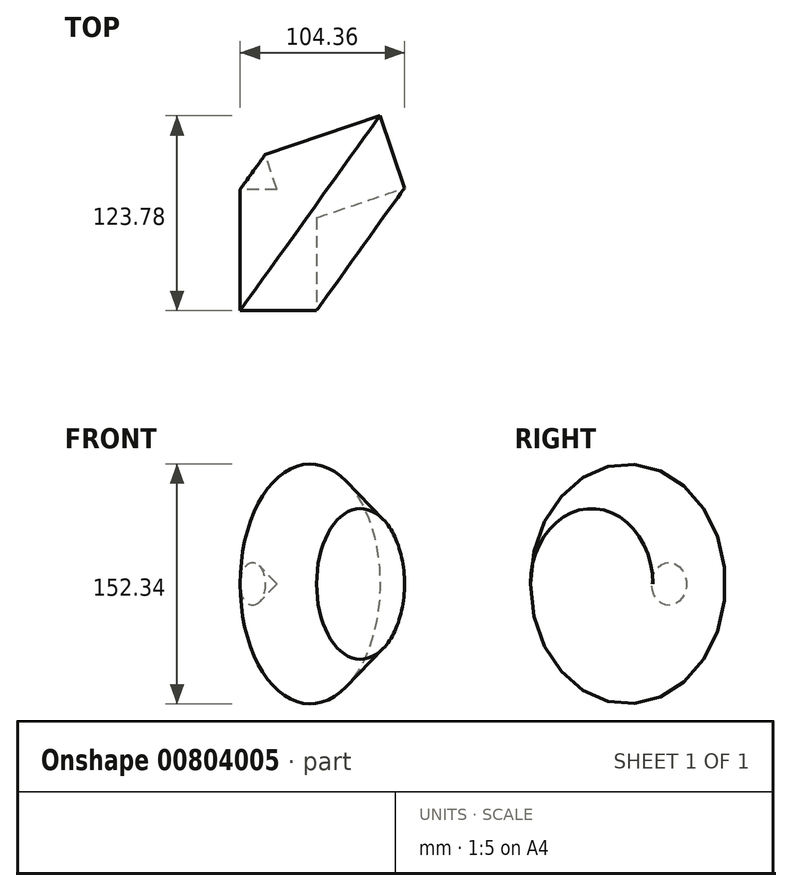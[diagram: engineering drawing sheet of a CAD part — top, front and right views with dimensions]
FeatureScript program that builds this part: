
annotation { "Feature Type Name" : "Feature", "Feature Type Description" : "" }
export const myFeature = defineFeature(function(context is Context, id is Id, definition is map)
    precondition{}
    {
        {
            var Q0;
            Q0=qCreatedBy(makeId("Top.planeOp"),FACE);
            var sketch = newSketch(context, id + "F0", { "sketchPlane" : qUnion([Q0])});
            skLineSegment(sketch, "E0.bottom", {"start": v(-26.72, 41.38) * mm, "end": v(21.83, 41.38) * mm});
            skLineSegment(sketch, "E0.top", {"start": v(-26.72, -35.58) * mm, "end": v(21.83, -35.58) * mm});
            skLineSegment(sketch, "E0.left", {"start": v(-26.72, 41.38) * mm, "end": v(-26.72, -35.58) * mm});
            skLineSegment(sketch, "E0.right", {"start": v(21.83, 41.38) * mm, "end": v(21.83, -35.58) * mm});
            skLineSegment(sketch, "E1", {"start": v(-14.81, 49.62) * mm, "end": v(39.24, 10.84) * mm});
            skSolve(sketch);
        }
        {
            var Q0;
            {var subQ1=sQuery(id+"F0.wireOp",EDGE,"E0.top");Q0=makeQuery(id+"F0.imprint","IMPRINT",FACE,{"disambiguationData":[TD([[makeQuery(id+"F0.imprint","IMPRINT",EDGE,{"derivedFrom":subQ1}),1.0]])]});}
            var Q1;
            Q1=sQuery(id+"F0.wireOp",EDGE,"E1");
            revolve(context, id + "F1", {"surfaceOperationType" : NewSurfaceOperationType.NEW, "entities" : qUnion([Q0]), "axis" : qUnion([Q1]), "revolveType" : RevolveType.FULL});
        }
    });
